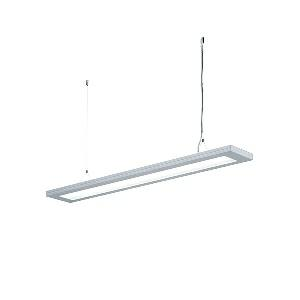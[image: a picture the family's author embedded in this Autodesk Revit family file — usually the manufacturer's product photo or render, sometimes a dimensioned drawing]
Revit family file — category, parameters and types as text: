
# Revit family: lavigo_-_dpp_9000_840_r_g2_00800469_8ee4
name_source: partatom
category: Lighting Fixtures
units: mm (PartAtom-declared; Revit-internal decimal feet)

## family parameters
Cut with Voids When Loaded = No
Host = Face
Light Source = No
Part Type = Normal
Room Calculation Point = No
Round Connector Dimension = Use Diameter
Shared = No

## types (1)
- LAVIGO - DPP 9000/840/R/G2 (1 x LED, 9350 lm, 4000K)
    Apparent Load = 65 VA
    Approval mark = CE
    CIE Flux Codes = 60 87 97 19 100
    Color Rendering = 80-89
    Color Temperature = 4000K
    Control Gear = Electronic ballast
    Default Elevation = 1800 mm
    Description = DPP 9000/840/R/G2|Suspended luminaire|light source: LED|connected load: 220-240V, 50/60Hz|Power consumption: approx. 65 W|standby: approx. 0,50|luminous flux: 9350 lm|luminous efficacy: 143 lm/W|light distribution: Direct/indirect|direct ratio: approx. 19 %|colour temperature: Cold white, ca. 4000 K|color rendering index (CRI): >= 80|chromaticity tolerance:  3 SDCM|System of protection: IP 20|technology: Presence and daylight sensor control (PIR)|luminaire body|material: Steel/plastic|surface: Powder coatet|colour: Silver metallic|lamp cover: Polycarbonate (PC), Clear|mains lead: 1.00 m With free stranded wires|Fastening: Steel cable 0.3 - 0.7 m|decorative contrast side parts: Flint grey|glare control: Prism aperture|luminance(L65): <= 2800 cd/m|unified glare rating(4H 8H): <=  16|special features: Canopy colour (pure white), Push button in luminaire head, Cradle to Cradle Certified TM, Direct light component with edge light and light-guide technology for homogenous light exit, Integrated light and presence sensor PIR, Retrofittable with TALK module, Separated, direct and indirect light individually adjustable|
    Frequency = 50 Hz
    Height = 36 mm
    Lamp = 1 x LED
    Lamp Light Flux = 9350 lm
    Lamp count = 1
    Length = 1245 mm
    Luminous efficacy = 144 lm/W
    Manufacturer = Waldmann
    ModVariant = No
    Model = 00800469
    Mounting Place = Ceiling
    Mounting Type = Pendant
    Number of Poles = 1
    OnlyDefault = Yes
    Power Factor = 1
    Product Name = LAVIGO - DPP 9000/840/R/G2
    Product group = Suspended luminaire
    ProductGroupID = 9
    Protection Class = Protection class I
    Protection Degree = IP 20
    RLX_Detail_Level = 1
    RLX_Emergency_Light_Flux = 0 lm
    RLX_Emergency_Type = 0
    RLX_Emergency_Type_DB = No
    RlxData = <blob elided: 25365 chars, md5=159da3b7>
    Socket = socket
    Standby Power = 0 W
    System Light Flux = 9350 lm
    System Power = 65 W
    Type Comments = Product without accessories
    Type Image = 121740000-00678747.jpg
    URL = http://relux.com
    VarID = ---
    Voltage = 230 V
    Voltage Range = 220-240 V
    Weight = 0.00 kg
    Width = 200 mm  [stored 0.656168 ft]

note: [stored X ft] marks values corroborated as IEEE doubles in the binary element streams (Revit-internal decimal feet)

## geometry (parser evidence)
native form markers: Blend x4, Sweep x13
no freeform markers — native parametric forms only
